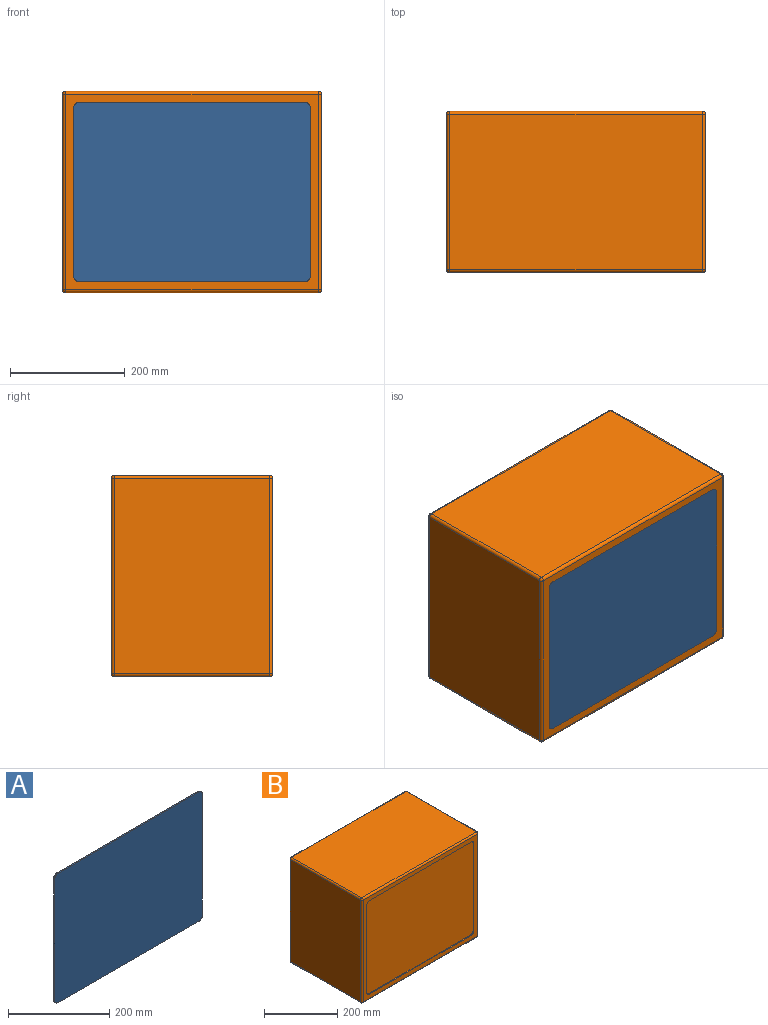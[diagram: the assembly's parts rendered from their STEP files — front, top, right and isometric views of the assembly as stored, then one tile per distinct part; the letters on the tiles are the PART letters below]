
ASSEMBLY  parts=2 mates=1
PART A: 10 faces, bbox 412x3x312 mm
  f0: plane 292x3mm, normal (1,0,0), area 876mm2, adj f1,f7,f8,f9
  f1: cylinder r=10mm len=10mm, axis (0,1,0), area 47.1mm2, adj f0,f2,f8,f9
  f2: plane 392x3mm, normal (0,0,1), area 1176mm2, adj f1,f3,f8,f9
  f3: cylinder r=10mm len=10mm, axis (0,1,0), area 47.1mm2, adj f2,f4,f8,f9
  f4: plane 292x3mm, normal (-1,0,0), area 876mm2, adj f3,f5,f8,f9
  f5: cylinder r=10mm len=10mm, axis (0,1,0), area 47.1mm2, adj f4,f6,f8,f9
  f6: plane 392x3mm, normal (0,0,-1), area 1176mm2, adj f5,f7,f8,f9
  f7: cylinder r=10mm len=10mm, axis (0,1,0), area 47.1mm2, adj f0,f6,f8,f9
  f8: plane 412x312mm, normal (0,-1,0), area 128458.2mm2, adj f0,f1,f2,f3,f4,f5,f6,f7
  f9: plane 412x312mm, normal (0,1,0), area 128458.2mm2, adj f0,f1,f2,f3,f4,f5,f6,f7
PART B: 35 faces, bbox 450x280x350 mm
  f0: plane 340x270mm, normal (-1,0,0), area 91800mm2, adj f14,f19,f22,f25
  f1: plane 440x340mm, normal (0,-1,0), area 21141.8mm2, adj f11,f20,f21,f25,f26,f27,f28,f29
  f2: plane 340x270mm, normal (1,0,0), area 91800mm2, adj f6,f10,f11,f12
  f3: plane 440x340mm, normal (0,1,0), area 149600mm2, adj f6,f9,f13,f14
  f4: plane 440x270mm, normal (0,0,1), area 118800mm2, adj f9,f10,f19,f20
  f5: plane 440x270mm, normal (0,0,-1), area 118800mm2, adj f12,f13,f21,f22
  f6: cylinder r=5mm len=340mm, axis (0,0,1), area 2670.4mm2, adj f2,f3,f7,f8
  f7: sphere r=5mm, area 39.3mm2, adj f6,f9,f10
  f8: sphere r=5mm, area 39.3mm2, adj f6,f12,f13
  f9: cylinder r=5mm len=440mm, axis (1,0,0), area 3455.8mm2, adj f3,f4,f7,f15
  f10: cylinder r=5mm len=270mm, axis (0,-1,0), area 2120.6mm2, adj f2,f4,f7,f16
  f11: cylinder r=5mm len=340mm, axis (0,0,-1), area 2670.4mm2, adj f1,f2,f16,f17
  f12: cylinder r=5mm len=270mm, axis (0,1,0), area 2120.6mm2, adj f2,f5,f8,f17
  f13: cylinder r=5mm len=440mm, axis (-1,0,0), area 3455.8mm2, adj f3,f5,f8,f18
  f14: cylinder r=5mm len=340mm, axis (0,0,-1), area 2670.4mm2, adj f0,f3,f15,f18
  f15: sphere r=5mm, area 39.3mm2, adj f9,f14,f19
  f16: sphere r=5mm, area 39.3mm2, adj f10,f11,f20
  f17: sphere r=5mm, area 39.3mm2, adj f11,f12,f21
  f18: sphere r=5mm, area 39.3mm2, adj f13,f14,f22
  f19: cylinder r=5mm len=270mm, axis (0,1,0), area 2120.6mm2, adj f0,f4,f15,f23
  f20: cylinder r=5mm len=440mm, axis (-1,0,0), area 3455.8mm2, adj f1,f4,f16,f23
  f21: cylinder r=5mm len=440mm, axis (1,0,0), area 3455.8mm2, adj f1,f5,f17,f24
  f22: cylinder r=5mm len=270mm, axis (0,-1,0), area 2120.6mm2, adj f0,f5,f18,f24
  f23: sphere r=5mm, area 39.3mm2, adj f19,f20,f25
  f24: sphere r=5mm, area 39.3mm2, adj f21,f22,f25
  f25: cylinder r=5mm len=340mm, axis (0,0,1), area 2670.4mm2, adj f0,f1,f23,f24
  f26: plane 292x3mm, normal (-1,0,0), area 876mm2, adj f1,f27,f33,f34
  f27: cylinder r=10mm len=10mm, axis (0,-1,0), area 47.1mm2, adj f1,f26,f28,f34
  f28: plane 392x3mm, normal (0,0,-1), area 1176mm2, adj f1,f27,f29,f34
  f29: cylinder r=10mm len=10mm, axis (0,-1,0), area 47.1mm2, adj f1,f28,f30,f34
  f30: plane 292x3mm, normal (1,0,0), area 876mm2, adj f1,f29,f31,f34
  f31: cylinder r=10mm len=10mm, axis (0,-1,0), area 47.1mm2, adj f1,f30,f32,f34
  f32: plane 392x3mm, normal (0,0,1), area 1176mm2, adj f1,f31,f33,f34
  f33: cylinder r=10mm len=10mm, axis (0,-1,0), area 47.1mm2, adj f1,f26,f32,f34
  f34: plane 412x312mm, normal (0,-1,0), area 128458.2mm2, adj f26,f27,f28,f29,f30,f31,f32,f33
PLACE A t=(-96.45,55.01,-8.96)mm
PLACE B t=(-96.45,55.01,-8.96)mm
MATE fastened A.f0 <-> B.f26  axis (1,0,0) through (109.55,-84.99,166.04)mm
